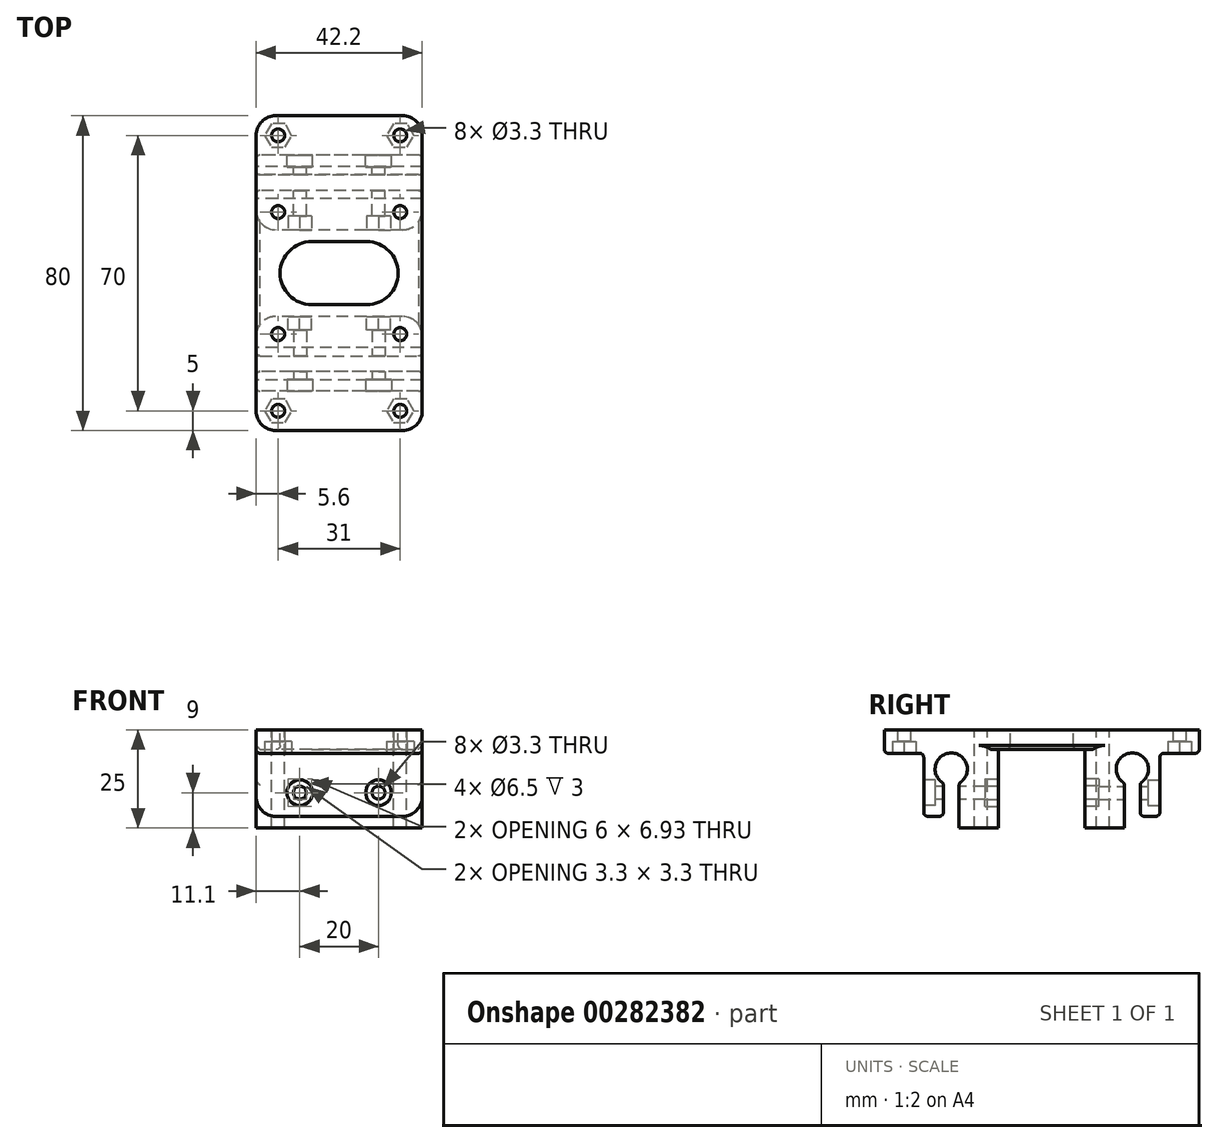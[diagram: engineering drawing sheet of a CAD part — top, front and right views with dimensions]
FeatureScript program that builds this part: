
annotation { "Feature Type Name" : "Feature", "Feature Type Description" : "" }
export const myFeature = defineFeature(function(context is Context, id is Id, definition is map)
    precondition{}
    {
        {
            var Q0;
            Q0=qCreatedBy(makeId("Right.planeOp"),FACE);
            var sketch = newSketch(context, id + "F0", { "sketchPlane" : qUnion([Q0])});
            skLineSegment(sketch, "E0.bottom", {"start": v(-10, 0) * mm, "end": v(-15, 0) * mm});
            skLineSegment(sketch, "E0.top", {"start": v(0, 22) * mm, "end": v(-80, 22) * mm});
            skLineSegment(sketch, "E0.left", {"start": v(0, 16) * mm, "end": v(0, 22) * mm});
            skLineSegment(sketch, "E0.right", {"start": v(-80, 16) * mm, "end": v(-80, 22) * mm});
            skLineSegment(sketch, "E1", {"start": v(0, 16) * mm, "end": v(-10, 16) * mm});
            skLineSegment(sketch, "E2", {"start": v(-10, 16) * mm, "end": v(-10, 0) * mm});
            skLineSegment(sketch, "E3", {"start": v(-80, 16) * mm, "end": v(-70, 16) * mm});
            skLineSegment(sketch, "E4", {"start": v(-70, 16) * mm, "end": v(-70, 0) * mm});
            skLineSegment(sketch, "E5", {"start": v(-10, 0) * mm, "end": v(0, 0) * mm, "construction": true});
            skLineSegment(sketch, "E6", {"start": v(0, 0) * mm, "end": v(0, 16) * mm, "construction": true});
            skLineSegment(sketch, "E7", {"start": v(-63, 22) * mm, "end": v(-63, 0) * mm, "construction": true});
            skLineSegment(sketch, "E8", {"start": v(-17, 22) * mm, "end": v(-17, 0) * mm, "construction": true});
            skArc(sketch, "E9", {"start": v(-61, 8.42) * mm, "mid": v(-63, 16.1) * mm, "end": v(-65, 8.42) * mm});
            skLineSegment(sketch, "E10", {"start": v(-63, 12) * mm, "end": v(-17, 12) * mm, "construction": true});
            skArc(sketch, "E11", {"start": v(-15, 8.42) * mm, "mid": v(-17, 16.1) * mm, "end": v(-19, 8.42) * mm});
            skLineSegment(sketch, "E12", {"start": v(-40, 22) * mm, "end": v(-40, -3) * mm, "construction": true});
            skLineSegment(sketch, "E13.top", {"start": v(-29, 17) * mm, "end": v(-51, 17) * mm});
            skLineSegment(sketch, "E13.left", {"start": v(-29, -3) * mm, "end": v(-29, 17) * mm});
            skLineSegment(sketch, "E13.right", {"start": v(-51, -3) * mm, "end": v(-51, 17) * mm});
            skLineSegment(sketch, "E14", {"start": v(-56, -3) * mm, "end": v(-56, 22) * mm, "construction": true});
            skLineSegment(sketch, "E15", {"start": v(-24, 22) * mm, "end": v(-24, -3) * mm, "construction": true});
            skLineSegment(sketch, "E16.0", {"start": v(-19, 8.42) * mm, "end": v(-19, -3) * mm});
            skLineSegment(sketch, "E17.0", {"start": v(-15, 8.42) * mm, "end": v(-15, 0) * mm});
            skLineSegment(sketch, "E18.0", {"start": v(-65, 8.42) * mm, "end": v(-65, 0) * mm});
            skLineSegment(sketch, "E19.0", {"start": v(-61, 8.42) * mm, "end": v(-61, -3) * mm});
            skLineSegment(sketch, "E20.trimOffspring", {"start": v(-65, 0) * mm, "end": v(-70, 0) * mm});
            skLineSegment(sketch, "E21", {"start": v(-61, -3) * mm, "end": v(-51, -3) * mm});
            skLineSegment(sketch, "E22.trimOffspring", {"start": v(-29, -3) * mm, "end": v(-19, -3) * mm});
            skSolve(sketch);
        }
        {
            var Q0;
            Q0=qSketchRegion(id+"F0",true);
            extrude(context, id + "F1", {"entities" : qUnion([Q0]), "depth" : 42.2 * mm});
        }
        {
            var Q0;
            Q0=makeQuery(id+"F1.opExtrude","SWEPT_FACE",FACE,{"disambiguationData":[OSD([sQuery(id+"F0.wireOp",EDGE,"E0.top")])]});
            var sketch = newSketch(context, id + "F2", { "sketchPlane" : qUnion([Q0])});
            skLineSegment(sketch, "E23", {"start": v(21.1, 0) * mm, "end": v(21.1, -80) * mm, "construction": true});
            skLineSegment(sketch, "E24.bottom", {"start": v(36.6, -24.5) * mm, "end": v(5.6, -24.5) * mm, "construction": true});
            skLineSegment(sketch, "E24.top", {"start": v(36.6, -55.5) * mm, "end": v(5.6, -55.5) * mm, "construction": true});
            skLineSegment(sketch, "E24.left", {"start": v(36.6, -24.5) * mm, "end": v(36.6, -55.5) * mm, "construction": true});
            skLineSegment(sketch, "E24.right", {"start": v(5.6, -24.5) * mm, "end": v(5.6, -55.5) * mm, "construction": true});
            skPoint(sketch, "E24.middle", {"position": v(21.1, -40) * mm});
            skCircle(sketch, "E25", {"center": v(5.6, -24.5) * mm, "radius": 1.65 * mm});
            skCircle(sketch, "E26", {"center": v(36.6, -24.5) * mm, "radius": 1.65 * mm});
            skCircle(sketch, "E27", {"center": v(36.6, -55.5) * mm, "radius": 1.65 * mm});
            skCircle(sketch, "E28", {"center": v(5.6, -55.5) * mm, "radius": 1.65 * mm});
            skLineSegment(sketch, "E29", {"start": v(28.1, -40) * mm, "end": v(14.1, -40) * mm, "construction": true});
            skArc(sketch, "E30.0.startCap", {"start": v(28.1, -32) * mm, "mid": v(36.1, -40) * mm, "end": v(28.1, -48) * mm});
            skArc(sketch, "E30.0.endCap", {"start": v(14.1, -48) * mm, "mid": v(6.1, -40) * mm, "end": v(14.1, -32) * mm});
            skLineSegment(sketch, "E30.0.left", {"start": v(28.1, -48) * mm, "end": v(14.1, -48) * mm});
            skLineSegment(sketch, "E30.0.right", {"start": v(28.1, -32) * mm, "end": v(14.1, -32) * mm});
            skSolve(sketch);
        }
        {
            var Q0;
            Q0=qSketchRegion(id+"F2",true);
            extrude(context, id + "F3", {"entities" : qUnion([Q0]), "operationType" : NewBodyOperationType.REMOVE, "endBound" : BoundingType.THROUGH_ALL, "oppositeDirection" : true, "depth" : 25 * mm});
        }
        {
            var Q0;
            Q0=makeQuery(id+"F1.opExtrude","CAP_EDGE",EDGE,{"disambiguationData":[OSD([sQuery(id+"F0.wireOp",EDGE,"E13.top")])],"isStart":false});
            var Q1;
            Q1=makeQuery(id+"F1.opExtrude","CAP_EDGE",EDGE,{"disambiguationData":[OSD([sQuery(id+"F0.wireOp",EDGE,"E13.top")])],"isStart":true});
            chamfer(context, id + "F4", {"entities" : qUnion([Q0, Q1]), "width" : 1 * mm, "tangentPropagation" : true});
        }
        {
            var Q0;
            Q0=makeQuery(id+"F1.opExtrude","CAP_EDGE",EDGE,{"disambiguationData":[OSD([sQuery(id+"F0.wireOp",EDGE,"E0.left")])],"isStart":true});
            var Q1;
            Q1=makeQuery(id+"F1.opExtrude","CAP_EDGE",EDGE,{"disambiguationData":[OSD([sQuery(id+"F0.wireOp",EDGE,"E0.left")])],"isStart":false});
            var Q2;
            Q2=makeQuery(id+"F1.opExtrude","CAP_EDGE",EDGE,{"disambiguationData":[OSD([sQuery(id+"F0.wireOp",EDGE,"E0.right")])],"isStart":true});
            var Q3;
            Q3=makeQuery(id+"F1.opExtrude","CAP_EDGE",EDGE,{"disambiguationData":[OSD([sQuery(id+"F0.wireOp",EDGE,"E0.right")])],"isStart":false});
            var Q4;
            Q4=makeQuery(id+"F1.opExtrude","CAP_EDGE",EDGE,{"disambiguationData":[OSD([sQuery(id+"F0.wireOp",EDGE,"E0.bottom")])],"isStart":true});
            var Q5;
            Q5=makeQuery(id+"F1.opExtrude","CAP_EDGE",EDGE,{"disambiguationData":[OSD([sQuery(id+"F0.wireOp",EDGE,"E0.bottom")])],"isStart":false});
            var Q6;
            Q6=makeQuery(id+"F1.opExtrude","CAP_EDGE",EDGE,{"disambiguationData":[OSD([sQuery(id+"F0.wireOp",EDGE,"E20.trimOffspring")])],"isStart":true});
            var Q7;
            Q7=makeQuery(id+"F1.opExtrude","CAP_EDGE",EDGE,{"disambiguationData":[OSD([sQuery(id+"F0.wireOp",EDGE,"E20.trimOffspring")])],"isStart":false});
            var Q8;
            Q8=makeQuery(id+"F1.opExtrude","CAP_EDGE",EDGE,{"disambiguationData":[OSD([sQuery(id+"F0.wireOp",EDGE,"E13.left")])],"isStart":true});
            var Q9;
            Q9=makeQuery(id+"F1.opExtrude","CAP_EDGE",EDGE,{"disambiguationData":[OSD([sQuery(id+"F0.wireOp",EDGE,"E13.right")])],"isStart":true});
            var Q10;
            Q10=makeQuery(id+"F1.opExtrude","CAP_EDGE",EDGE,{"disambiguationData":[OSD([sQuery(id+"F0.wireOp",EDGE,"E13.left")])],"isStart":false});
            var Q11;
            Q11=makeQuery(id+"F1.opExtrude","CAP_EDGE",EDGE,{"disambiguationData":[OSD([sQuery(id+"F0.wireOp",EDGE,"E13.right")])],"isStart":false});
            fillet(context, id + "F5", {"entities" : qUnion([Q0, Q1, Q2, Q3, Q4, Q5, Q6, Q7, Q8, Q9, Q10, Q11]), "radius" : 5 * mm, "tangentPropagation" : true, "allowEdgeOverflow" : false});
        }
        {
            var Q0;
            Q0=makeQuery(id+"F1.opExtrude","SWEPT_FACE",FACE,{"disambiguationData":[OSD([sQuery(id+"F0.wireOp",EDGE,"E1")])]});
            var sketch = newSketch(context, id + "F6", { "sketchPlane" : qUnion([Q0])});
            skLineSegment(sketch, "E31", {"start": v(21.1, 0) * mm, "end": v(21.1, 80) * mm, "construction": true});
            skLineSegment(sketch, "E32", {"start": v(21.1, 40) * mm, "end": v(36.6, 40) * mm, "construction": true});
            skPoint(sketch, "E32.endSnap0", {"position": v(21.1, 40) * mm});
            skLineSegment(sketch, "E33", {"start": v(21.1, 40) * mm, "end": v(5.6, 40) * mm, "construction": true});
            skLineSegment(sketch, "E34.0", {"start": v(21.1, 5) * mm, "end": v(36.6, 5) * mm, "construction": true});
            skLineSegment(sketch, "E34.1", {"start": v(21.1, 5) * mm, "end": v(5.6, 5) * mm, "construction": true});
            skLineSegment(sketch, "E35.MirrorCS", {"start": v(21.1, 75) * mm, "end": v(36.6, 75) * mm, "construction": true});
            skLineSegment(sketch, "E36.MirrorCS", {"start": v(21.1, 75) * mm, "end": v(5.6, 75) * mm, "construction": true});
            skCircle(sketch, "E37.cCircle", {"center": v(5.6, 5) * mm, "radius": 3 * mm, "construction": true});
            skLineSegment(sketch, "E37.0", {"start": v(7.33, 2) * mm, "end": v(3.87, 2) * mm});
            skLineSegment(sketch, "E37.1", {"start": v(3.87, 2) * mm, "end": v(2.14, 5) * mm});
            skLineSegment(sketch, "E37.2", {"start": v(2.14, 5) * mm, "end": v(3.87, 8) * mm});
            skLineSegment(sketch, "E37.3", {"start": v(3.87, 8) * mm, "end": v(7.33, 8) * mm});
            skLineSegment(sketch, "E37.4", {"start": v(7.33, 8) * mm, "end": v(9.06, 5) * mm});
            skLineSegment(sketch, "E37.5", {"start": v(9.06, 5) * mm, "end": v(7.33, 2) * mm});
            skPoint(sketch, "E37.0.midPoint", {"position": v(5.6, 2) * mm});
            skCircle(sketch, "E38.cCircle", {"center": v(36.6, 5) * mm, "radius": 3 * mm, "construction": true});
            skLineSegment(sketch, "E38.0", {"start": v(38.33, 2) * mm, "end": v(34.87, 2) * mm});
            skLineSegment(sketch, "E38.1", {"start": v(34.87, 2) * mm, "end": v(33.14, 5) * mm});
            skLineSegment(sketch, "E38.2", {"start": v(33.14, 5) * mm, "end": v(34.87, 8) * mm});
            skLineSegment(sketch, "E38.3", {"start": v(34.87, 8) * mm, "end": v(38.33, 8) * mm});
            skLineSegment(sketch, "E38.4", {"start": v(38.33, 8) * mm, "end": v(40.06, 5) * mm});
            skLineSegment(sketch, "E38.5", {"start": v(40.06, 5) * mm, "end": v(38.33, 2) * mm});
            skPoint(sketch, "E38.0.midPoint", {"position": v(36.6, 2) * mm});
            skCircle(sketch, "E39.cCircle", {"center": v(5.6, 75) * mm, "radius": 3 * mm, "construction": true});
            skLineSegment(sketch, "E39.0", {"start": v(7.33, 72) * mm, "end": v(3.87, 72) * mm});
            skLineSegment(sketch, "E39.1", {"start": v(3.87, 72) * mm, "end": v(2.14, 75) * mm});
            skLineSegment(sketch, "E39.2", {"start": v(2.14, 75) * mm, "end": v(3.87, 78) * mm});
            skLineSegment(sketch, "E39.3", {"start": v(3.87, 78) * mm, "end": v(7.33, 78) * mm});
            skLineSegment(sketch, "E39.4", {"start": v(7.33, 78) * mm, "end": v(9.06, 75) * mm});
            skLineSegment(sketch, "E39.5", {"start": v(9.06, 75) * mm, "end": v(7.33, 72) * mm});
            skPoint(sketch, "E39.0.midPoint", {"position": v(5.6, 72) * mm});
            skCircle(sketch, "E40.cCircle", {"center": v(36.6, 75) * mm, "radius": 3 * mm, "construction": true});
            skLineSegment(sketch, "E40.0", {"start": v(38.33, 72) * mm, "end": v(34.87, 72) * mm});
            skLineSegment(sketch, "E40.1", {"start": v(34.87, 72) * mm, "end": v(33.14, 75) * mm});
            skLineSegment(sketch, "E40.2", {"start": v(33.14, 75) * mm, "end": v(34.87, 78) * mm});
            skLineSegment(sketch, "E40.3", {"start": v(34.87, 78) * mm, "end": v(38.33, 78) * mm});
            skLineSegment(sketch, "E40.4", {"start": v(38.33, 78) * mm, "end": v(40.06, 75) * mm});
            skLineSegment(sketch, "E40.5", {"start": v(40.06, 75) * mm, "end": v(38.33, 72) * mm});
            skPoint(sketch, "E40.0.midPoint", {"position": v(36.6, 72) * mm});
            skSolve(sketch);
        }
        {
            var Q0;
            Q0=qSketchRegion(id+"F6",true);
            extrude(context, id + "F7", {"entities" : qUnion([Q0]), "operationType" : NewBodyOperationType.REMOVE, "oppositeDirection" : true, "depth" : 3 * mm});
        }
        {
            var Q0;
            Q0=sQuery(id+"F6.wireOp",VERTEX,"E37.cCircle.center");
            var Q1;
            Q1=sQuery(id+"F6.wireOp",VERTEX,"E38.cCircle.center");
            var Q2;
            Q2=sQuery(id+"F6.wireOp",VERTEX,"E40.cCircle.center");
            var Q3;
            Q3=sQuery(id+"F6.wireOp",VERTEX,"E39.cCircle.center");
            var Q4;
            Q4=makeQuery(id+"F1.opExtrude","SWEPT_BODY",BODY,{"disambiguationData":[OSD([sQuery(id+"F0.wireOp",EDGE,"E0.bottom"),sQuery(id+"F0.wireOp",EDGE,"E0.top"),sQuery(id+"F0.wireOp",EDGE,"E0.left"),sQuery(id+"F0.wireOp",EDGE,"E0.right"),sQuery(id+"F0.wireOp",EDGE,"E1"),sQuery(id+"F0.wireOp",EDGE,"E2"),sQuery(id+"F0.wireOp",EDGE,"E3"),sQuery(id+"F0.wireOp",EDGE,"E4"),sQuery(id+"F0.wireOp",EDGE,"E9"),sQuery(id+"F0.wireOp",EDGE,"E11"),sQuery(id+"F0.wireOp",EDGE,"E13.top"),sQuery(id+"F0.wireOp",EDGE,"E13.left"),sQuery(id+"F0.wireOp",EDGE,"E13.right"),sQuery(id+"F0.wireOp",EDGE,"E16.0"),sQuery(id+"F0.wireOp",EDGE,"E17.0"),sQuery(id+"F0.wireOp",EDGE,"E18.0"),sQuery(id+"F0.wireOp",EDGE,"E19.0"),sQuery(id+"F0.wireOp",EDGE,"E20.trimOffspring"),sQuery(id+"F0.wireOp",EDGE,"E21"),sQuery(id+"F0.wireOp",EDGE,"E22.trimOffspring")])]});
            hole(context, id + "F8", {"style" : HoleStyle.SIMPLE, "endStyle" : HoleEndStyle.THROUGH, "standardTappedOrClearance" : lookupTablePath({ "standard" : "ISO", "fit" : "Normal", "size" : "M3", "type" : "Clearance" }), "standardBlindInLast" : lookupTablePath({ "fit" : "Standard", "standard" : "ISO", "size" : "M3", "type" : "Clearance" }), "holeDiameter" : 3.3 * mm, "tappedDepth" : 3 * mm, "tapClearance" : 3, "startFromSketch" : true, "locations" : qUnion([Q0, Q1, Q2, Q3]), "scope" : qUnion([Q4])});
        }
        {
            var Q0;
            Q0=makeQuery(id+"F1.opExtrude","SWEPT_FACE",FACE,{"disambiguationData":[OSD([sQuery(id+"F0.wireOp",EDGE,"E2")])]});
            var sketch = newSketch(context, id + "F9", { "sketchPlane" : qUnion([Q0])});
            skLineSegment(sketch, "E41", {"start": v(-42.2, 6) * mm, "end": v(0, 6) * mm, "construction": true});
            skLineSegment(sketch, "E42", {"start": v(-21.1, 6) * mm, "end": v(-21.1, 0) * mm, "construction": true});
            skPoint(sketch, "E43", {"position": v(-31.1, 6) * mm});
            skPoint(sketch, "E44", {"position": v(-11.1, 6) * mm});
            skSolve(sketch);
        }
        {
            var Q0;
            Q0=sQuery(id+"F9.wireOp",VERTEX,"E43");
            var Q1;
            Q1=sQuery(id+"F9.wireOp",VERTEX,"E44");
            var Q2;
            Q2=makeQuery(id+"F1.opExtrude","SWEPT_BODY",BODY,{"disambiguationData":[OSD([sQuery(id+"F0.wireOp",EDGE,"E0.bottom"),sQuery(id+"F0.wireOp",EDGE,"E0.top"),sQuery(id+"F0.wireOp",EDGE,"E0.left"),sQuery(id+"F0.wireOp",EDGE,"E0.right"),sQuery(id+"F0.wireOp",EDGE,"E1"),sQuery(id+"F0.wireOp",EDGE,"E2"),sQuery(id+"F0.wireOp",EDGE,"E3"),sQuery(id+"F0.wireOp",EDGE,"E4"),sQuery(id+"F0.wireOp",EDGE,"E9"),sQuery(id+"F0.wireOp",EDGE,"E11"),sQuery(id+"F0.wireOp",EDGE,"E13.top"),sQuery(id+"F0.wireOp",EDGE,"E13.left"),sQuery(id+"F0.wireOp",EDGE,"E13.right"),sQuery(id+"F0.wireOp",EDGE,"E16.0"),sQuery(id+"F0.wireOp",EDGE,"E17.0"),sQuery(id+"F0.wireOp",EDGE,"E18.0"),sQuery(id+"F0.wireOp",EDGE,"E19.0"),sQuery(id+"F0.wireOp",EDGE,"E20.trimOffspring"),sQuery(id+"F0.wireOp",EDGE,"E21"),sQuery(id+"F0.wireOp",EDGE,"E22.trimOffspring")])]});
            hole(context, id + "F10", {"style" : HoleStyle.C_BORE, "endStyle" : HoleEndStyle.BLIND, "standardTappedOrClearance" : lookupTablePath({ "standard" : "ISO", "fit" : "Normal", "size" : "M3", "type" : "Clearance" }), "standardBlindInLast" : lookupTablePath({ "fit" : "Standard", "standard" : "ISO", "size" : "M3", "type" : "Clearance" }), "holeDiameter" : 3.3 * mm, "cBoreDiameter" : 6.5 * mm, "cBoreDepth" : 3 * mm, "holeDepth" : 20 * mm, "tappedDepth" : 3 * mm, "tapClearance" : 3, "startFromSketch" : true, "locations" : qUnion([Q0, Q1]), "scope" : qUnion([Q2])});
        }
        {
            var Q0;
            Q0=makeQuery(id+"F1.opExtrude","SWEPT_FACE",FACE,{"disambiguationData":[OSD([sQuery(id+"F0.wireOp",EDGE,"E4")])]});
            var sketch = newSketch(context, id + "F11", { "sketchPlane" : qUnion([Q0])});
            skLineSegment(sketch, "E45", {"start": v(0, 6) * mm, "end": v(42.2, 6) * mm, "construction": true});
            skLineSegment(sketch, "E46", {"start": v(21.1, 6) * mm, "end": v(21.1, 0) * mm, "construction": true});
            skPoint(sketch, "E47", {"position": v(11.1, 6) * mm});
            skPoint(sketch, "E48", {"position": v(31.1, 6) * mm});
            skSolve(sketch);
        }
        {
            var Q0;
            Q0=sQuery(id+"F11.wireOp",VERTEX,"E47");
            var Q1;
            Q1=sQuery(id+"F11.wireOp",VERTEX,"E48");
            var Q2;
            Q2=makeQuery(id+"F1.opExtrude","SWEPT_BODY",BODY,{"disambiguationData":[OSD([sQuery(id+"F0.wireOp",EDGE,"E0.bottom"),sQuery(id+"F0.wireOp",EDGE,"E0.top"),sQuery(id+"F0.wireOp",EDGE,"E0.left"),sQuery(id+"F0.wireOp",EDGE,"E0.right"),sQuery(id+"F0.wireOp",EDGE,"E1"),sQuery(id+"F0.wireOp",EDGE,"E2"),sQuery(id+"F0.wireOp",EDGE,"E3"),sQuery(id+"F0.wireOp",EDGE,"E4"),sQuery(id+"F0.wireOp",EDGE,"E9"),sQuery(id+"F0.wireOp",EDGE,"E11"),sQuery(id+"F0.wireOp",EDGE,"E13.top"),sQuery(id+"F0.wireOp",EDGE,"E13.left"),sQuery(id+"F0.wireOp",EDGE,"E13.right"),sQuery(id+"F0.wireOp",EDGE,"E16.0"),sQuery(id+"F0.wireOp",EDGE,"E17.0"),sQuery(id+"F0.wireOp",EDGE,"E18.0"),sQuery(id+"F0.wireOp",EDGE,"E19.0"),sQuery(id+"F0.wireOp",EDGE,"E20.trimOffspring"),sQuery(id+"F0.wireOp",EDGE,"E21"),sQuery(id+"F0.wireOp",EDGE,"E22.trimOffspring")])]});
            hole(context, id + "F12", {"style" : HoleStyle.C_BORE, "endStyle" : HoleEndStyle.BLIND, "standardTappedOrClearance" : lookupTablePath({ "standard" : "ISO", "fit" : "Normal", "size" : "M3", "type" : "Clearance" }), "standardBlindInLast" : lookupTablePath({ "fit" : "Standard", "standard" : "ISO", "size" : "M3", "type" : "Clearance" }), "holeDiameter" : 3.3 * mm, "cBoreDiameter" : 6.5 * mm, "cBoreDepth" : 3 * mm, "holeDepth" : 20 * mm, "tappedDepth" : 3 * mm, "tapClearance" : 3, "startFromSketch" : true, "locations" : qUnion([Q0, Q1]), "scope" : qUnion([Q2])});
        }
        {
            var Q0;
            Q0=makeQuery(id+"F1.opExtrude","SWEPT_FACE",FACE,{"disambiguationData":[OSD([sQuery(id+"F0.wireOp",EDGE,"E13.right")])]});
            var sketch = newSketch(context, id + "F13", { "sketchPlane" : qUnion([Q0])});
            skCircle(sketch, "E49.cCircle", {"center": v(-11.1, 6) * mm, "radius": 3 * mm, "construction": true});
            skLineSegment(sketch, "E49.0", {"start": v(-8.1, 7.73) * mm, "end": v(-8.1, 4.27) * mm});
            skLineSegment(sketch, "E49.1", {"start": v(-8.1, 4.27) * mm, "end": v(-11.1, 2.54) * mm});
            skLineSegment(sketch, "E49.2", {"start": v(-11.1, 2.54) * mm, "end": v(-14.1, 4.27) * mm});
            skLineSegment(sketch, "E49.3", {"start": v(-14.1, 4.27) * mm, "end": v(-14.1, 7.73) * mm});
            skLineSegment(sketch, "E49.4", {"start": v(-14.1, 7.73) * mm, "end": v(-11.1, 9.46) * mm});
            skLineSegment(sketch, "E49.5", {"start": v(-11.1, 9.46) * mm, "end": v(-8.1, 7.73) * mm});
            skPoint(sketch, "E49.0.midPoint", {"position": v(-8.1, 6) * mm});
            skCircle(sketch, "E50.cCircle", {"center": v(-31.1, 6) * mm, "radius": 3 * mm, "construction": true});
            skLineSegment(sketch, "E50.0", {"start": v(-28.1, 7.73) * mm, "end": v(-28.1, 4.27) * mm});
            skLineSegment(sketch, "E50.1", {"start": v(-28.1, 4.27) * mm, "end": v(-31.1, 2.54) * mm});
            skLineSegment(sketch, "E50.2", {"start": v(-31.1, 2.54) * mm, "end": v(-34.1, 4.27) * mm});
            skLineSegment(sketch, "E50.3", {"start": v(-34.1, 4.27) * mm, "end": v(-34.1, 7.73) * mm});
            skLineSegment(sketch, "E50.4", {"start": v(-34.1, 7.73) * mm, "end": v(-31.1, 9.46) * mm});
            skLineSegment(sketch, "E50.5", {"start": v(-31.1, 9.46) * mm, "end": v(-28.1, 7.73) * mm});
            skPoint(sketch, "E50.0.midPoint", {"position": v(-28.1, 6) * mm});
            skSolve(sketch);
        }
        {
            var Q0;
            Q0=qSketchRegion(id+"F13",true);
            extrude(context, id + "F14", {"entities" : qUnion([Q0]), "operationType" : NewBodyOperationType.REMOVE, "oppositeDirection" : true, "depth" : 3.5 * mm});
        }
        {
            var Q0;
            Q0=makeQuery(id+"F1.opExtrude","SWEPT_FACE",FACE,{"disambiguationData":[OSD([sQuery(id+"F0.wireOp",EDGE,"E13.left")])]});
            var sketch = newSketch(context, id + "F15", { "sketchPlane" : qUnion([Q0])});
            skCircle(sketch, "E51.cCircle", {"center": v(31.1, 6) * mm, "radius": 3 * mm, "construction": true});
            skLineSegment(sketch, "E51.0", {"start": v(28.1, 4.27) * mm, "end": v(28.1, 7.73) * mm});
            skLineSegment(sketch, "E51.1", {"start": v(28.1, 7.73) * mm, "end": v(31.1, 9.46) * mm});
            skLineSegment(sketch, "E51.2", {"start": v(31.1, 9.46) * mm, "end": v(34.1, 7.73) * mm});
            skLineSegment(sketch, "E51.3", {"start": v(34.1, 7.73) * mm, "end": v(34.1, 4.27) * mm});
            skLineSegment(sketch, "E51.4", {"start": v(34.1, 4.27) * mm, "end": v(31.1, 2.54) * mm});
            skLineSegment(sketch, "E51.5", {"start": v(31.1, 2.54) * mm, "end": v(28.1, 4.27) * mm});
            skPoint(sketch, "E51.0.midPoint", {"position": v(28.1, 6) * mm});
            skCircle(sketch, "E52.cCircle", {"center": v(11.1, 6) * mm, "radius": 3 * mm, "construction": true});
            skLineSegment(sketch, "E52.0", {"start": v(8.1, 4.27) * mm, "end": v(8.1, 7.73) * mm});
            skLineSegment(sketch, "E52.1", {"start": v(8.1, 7.73) * mm, "end": v(11.1, 9.46) * mm});
            skLineSegment(sketch, "E52.2", {"start": v(11.1, 9.46) * mm, "end": v(14.1, 7.73) * mm});
            skLineSegment(sketch, "E52.3", {"start": v(14.1, 7.73) * mm, "end": v(14.1, 4.27) * mm});
            skLineSegment(sketch, "E52.4", {"start": v(14.1, 4.27) * mm, "end": v(11.1, 2.54) * mm});
            skLineSegment(sketch, "E52.5", {"start": v(11.1, 2.54) * mm, "end": v(8.1, 4.27) * mm});
            skPoint(sketch, "E52.0.midPoint", {"position": v(8.1, 6) * mm});
            skSolve(sketch);
        }
        {
            var Q0;
            Q0=qSketchRegion(id+"F15",true);
            extrude(context, id + "F16", {"entities" : qUnion([Q0]), "operationType" : NewBodyOperationType.REMOVE, "oppositeDirection" : true, "depth" : 3.5 * mm});
        }
        {
            var Q0;
            Q0=makeQuery(id+"F1.opExtrude","SWEPT_EDGE",EDGE,{"disambiguationData":[OSD([sQuery(id+"F0.wireOp",EDGE,"E1"),sQuery(id+"F0.wireOp",EDGE,"E2")])]});
            var Q1;
            Q1=makeQuery(id+"F1.opExtrude","SWEPT_EDGE",EDGE,{"disambiguationData":[OSD([sQuery(id+"F0.wireOp",EDGE,"E3"),sQuery(id+"F0.wireOp",EDGE,"E4")])]});
            var Q2;
            Q2=makeQuery(id+"F1.opExtrude","SWEPT_EDGE",EDGE,{"disambiguationData":[OSD([sQuery(id+"F0.wireOp",EDGE,"E11"),sQuery(id+"F0.wireOp",EDGE,"E17.0")])]});
            var Q3;
            Q3=makeQuery(id+"F1.opExtrude","SWEPT_EDGE",EDGE,{"disambiguationData":[OSD([sQuery(id+"F0.wireOp",EDGE,"E9"),sQuery(id+"F0.wireOp",EDGE,"E18.0")])]});
            var Q4;
            Q4=makeQuery(id+"F3.boolean.opBoolean","INTERSECT",EDGE,{"derivedFrom":[makeQuery(id+"F1.opExtrude","SWEPT_FACE",FACE,{"disambiguationData":[OSD([sQuery(id+"F0.wireOp",EDGE,"E13.top")])]}),makeQuery(id+"F3.opExtrude","SWEPT_FACE",FACE,{"disambiguationData":[OSD([sQuery(id+"F2.wireOp",EDGE,"E30.0.endCap")])]})]});
            var Q5;
            Q5=makeQuery(id+"F1.opExtrude","CAP_EDGE",EDGE,{"disambiguationData":[OSD([sQuery(id+"F0.wireOp",EDGE,"E16.0")])],"isStart":false});
            var Q6;
            Q6=makeQuery(id+"F1.opExtrude","CAP_EDGE",EDGE,{"disambiguationData":[OSD([sQuery(id+"F0.wireOp",EDGE,"E19.0")])],"isStart":false});
            var Q7;
            Q7=makeQuery(id+"F1.opExtrude","CAP_EDGE",EDGE,{"disambiguationData":[OSD([sQuery(id+"F0.wireOp",EDGE,"E19.0")])],"isStart":true});
            var Q8;
            Q8=makeQuery(id+"F1.opExtrude","CAP_EDGE",EDGE,{"disambiguationData":[OSD([sQuery(id+"F0.wireOp",EDGE,"E16.0")])],"isStart":true});
            var Q9;
            Q9=makeQuery(id+"F1.opExtrude","SWEPT_EDGE",EDGE,{"disambiguationData":[OSD([sQuery(id+"F0.wireOp",EDGE,"E9"),sQuery(id+"F0.wireOp",EDGE,"E19.0")])]});
            var Q10;
            Q10=makeQuery(id+"F1.opExtrude","SWEPT_EDGE",EDGE,{"disambiguationData":[OSD([sQuery(id+"F0.wireOp",EDGE,"E11"),sQuery(id+"F0.wireOp",EDGE,"E16.0")])]});
            fillet(context, id + "F17", {"entities" : qUnion([Q0, Q1, Q2, Q3, Q4, Q5, Q6, Q7, Q8, Q9, Q10]), "radius" : 1 * mm, "tangentPropagation" : true, "allowEdgeOverflow" : false});
        }
        {
            var Q0;
            Q0=makeQuery(id+"F1.opExtrude","CAP_EDGE",EDGE,{"disambiguationData":[OSD([sQuery(id+"F0.wireOp",EDGE,"E2")])],"isStart":true});
            var Q1;
            Q1=makeQuery(id+"F1.opExtrude","SWEPT_EDGE",EDGE,{"disambiguationData":[OSD([sQuery(id+"F0.wireOp",EDGE,"E0.right"),sQuery(id+"F0.wireOp",EDGE,"E3")])]});
            fillet(context, id + "F18", {"entities" : qUnion([Q0, Q1]), "radius" : 1 * mm, "tangentPropagation" : true, "allowEdgeOverflow" : false});
        }
        {
            var Q0;
            Q0=makeQuery(id+"F1.opExtrude","CAP_EDGE",EDGE,{"disambiguationData":[OSD([sQuery(id+"F0.wireOp",EDGE,"E18.0")])],"isStart":false});
            var Q1;
            Q1=makeQuery(id+"F5.opFillet","BLEND_EDGE",EDGE,{"blendedFrom":[makeQuery(id+"F1.opExtrude","CAP_EDGE",EDGE,{"disambiguationData":[OSD([sQuery(id+"F0.wireOp",EDGE,"E20.trimOffspring")])],"isStart":false}),makeQuery(id+"F1.opExtrude","SWEPT_FACE",FACE,{"disambiguationData":[OSD([sQuery(id+"F0.wireOp",EDGE,"E18.0")])]})],"blendedInto":[makeQuery(id+"F1.opExtrude","SWEPT_FACE",FACE,{"disambiguationData":[OSD([sQuery(id+"F0.wireOp",EDGE,"E18.0")])]})]});
            var Q2;
            Q2=makeQuery(id+"F1.opExtrude","SWEPT_EDGE",EDGE,{"disambiguationData":[OSD([sQuery(id+"F0.wireOp",EDGE,"E18.0"),sQuery(id+"F0.wireOp",EDGE,"E20.trimOffspring")])]});
            var Q3;
            Q3=makeQuery(id+"F5.opFillet","BLEND_EDGE",EDGE,{"blendedFrom":[makeQuery(id+"F1.opExtrude","CAP_EDGE",EDGE,{"disambiguationData":[OSD([sQuery(id+"F0.wireOp",EDGE,"E20.trimOffspring")])],"isStart":true}),makeQuery(id+"F1.opExtrude","SWEPT_FACE",FACE,{"disambiguationData":[OSD([sQuery(id+"F0.wireOp",EDGE,"E18.0")])]})],"blendedInto":[makeQuery(id+"F1.opExtrude","SWEPT_FACE",FACE,{"disambiguationData":[OSD([sQuery(id+"F0.wireOp",EDGE,"E18.0")])]})]});
            var Q4;
            Q4=makeQuery(id+"F1.opExtrude","CAP_EDGE",EDGE,{"disambiguationData":[OSD([sQuery(id+"F0.wireOp",EDGE,"E18.0")])],"isStart":true});
            var Q5;
            Q5=makeQuery(id+"F1.opExtrude","CAP_EDGE",EDGE,{"disambiguationData":[OSD([sQuery(id+"F0.wireOp",EDGE,"E17.0")])],"isStart":true});
            var Q6;
            Q6=makeQuery(id+"F5.opFillet","BLEND_EDGE",EDGE,{"blendedFrom":[makeQuery(id+"F1.opExtrude","CAP_EDGE",EDGE,{"disambiguationData":[OSD([sQuery(id+"F0.wireOp",EDGE,"E0.bottom")])],"isStart":true}),makeQuery(id+"F1.opExtrude","SWEPT_FACE",FACE,{"disambiguationData":[OSD([sQuery(id+"F0.wireOp",EDGE,"E17.0")])]})],"blendedInto":[makeQuery(id+"F1.opExtrude","SWEPT_FACE",FACE,{"disambiguationData":[OSD([sQuery(id+"F0.wireOp",EDGE,"E17.0")])]})]});
            var Q7;
            Q7=makeQuery(id+"F1.opExtrude","SWEPT_EDGE",EDGE,{"disambiguationData":[OSD([sQuery(id+"F0.wireOp",EDGE,"E0.bottom"),sQuery(id+"F0.wireOp",EDGE,"E17.0")])]});
            var Q8;
            Q8=makeQuery(id+"F5.opFillet","BLEND_EDGE",EDGE,{"blendedFrom":[makeQuery(id+"F1.opExtrude","CAP_EDGE",EDGE,{"disambiguationData":[OSD([sQuery(id+"F0.wireOp",EDGE,"E0.bottom")])],"isStart":false}),makeQuery(id+"F1.opExtrude","SWEPT_FACE",FACE,{"disambiguationData":[OSD([sQuery(id+"F0.wireOp",EDGE,"E17.0")])]})],"blendedInto":[makeQuery(id+"F1.opExtrude","SWEPT_FACE",FACE,{"disambiguationData":[OSD([sQuery(id+"F0.wireOp",EDGE,"E17.0")])]})]});
            var Q9;
            Q9=makeQuery(id+"F1.opExtrude","CAP_EDGE",EDGE,{"disambiguationData":[OSD([sQuery(id+"F0.wireOp",EDGE,"E17.0")])],"isStart":false});
            fillet(context, id + "F19", {"entities" : qUnion([Q0, Q1, Q2, Q3, Q4, Q5, Q6, Q7, Q8, Q9]), "radius" : 1 * mm, "allowEdgeOverflow" : false});
        }
    });
